# Revit family: URA SPOT Autotest - Permanent_Non Permanent
name_source: partatom
category: Luminaires
units: mm (PartAtom-declared; Revit-internal decimal feet)

## family parameters
Cote de connecteur circulaire = Utiliser le diamètre
Couper avec des vides une fois chargée = Non
Hôte = Face
Partagée = Non
Repere pour localisation dans la piece = Non
Source d'éclairage = Non
Type d'élément = Normal

## types (5) — shared parameters
Alimentation de secours = Autonome (batterie individuelle)
Classe de protection = II
Conditions Générale d'Utilisation = https://export.legrand.com
Consommation en veille = 0.0 mA
Couleur = Blanc
Diamètre = 125 mm
Elévation par défaut = 2300 mm
Fabricant = LEGRAND
Fonction = Éclairage d'évacuation et d'ambiance
Fréquence = 50-60
Hauteur = 45 mm
Hauteur encastrement = 42 mm
IK = 07
IP = 42
Matière = Plastique
Mode de pose = Encastré
Objet Connecté = Non
Puissance du système = 2 W
Temperature d'utilisation MIN-MAX = -5-35
Tension = 230 AC/DC
Type de connexion = Raccordement à vis
Type de pictogramme = autre
URL = https://www.legrand.com
capacité des bornes = 1,5-2,5
source lumineuse = LED non interchangeable
état des accus = NiMh

## per-type parameters (varying)
| type | Autonomie | Batterie de rechange | Désignation produit | Flux lumineux utile | Référence / Modèle | Système de contrôle | Type de commutation |
| 100LM-1H | 1H | 660182 | BAES U22ROND ENCASTRE PERMANENT - NON PERMANENT 100 LUMENS 1H AUTOTEST | 100 lm | LG-660142 | Auto-test automatique | Permanent |
| 200LM-1H | 1H | 660182 | BAES U22ROND ENCASTRE PERMANENT - NON PERMANENT 200 LUMENS 1H AUTOTEST | 200 lm | LG-660144 | Auto-test automatique | Permanent |
| 350LM-1H | 1H | 660184 | BAES U22ROND ENCASTRE PERMANENT - NON PERMANENT 350 LUMENS 1H AUTOTEST | 350 lm | LG-660145 | Auto-test automatique | Permanent |
| 100LM-3H | 3H | 660182 | BAES U22ROND  PERMANENT NON PERMANENT 100 LUMENS 3 H AUTOTEST | 100 lm | LG-660146 | sans | Non permanent |
| 200LM-2H | 2H | 660184 | BAES U22ROND ENCASTRE PERMANENT - NON PERMANENT 200 LUMENS 2H AUTOTEST | 200 lm | LG-660147 | Auto-test automatique | Permanent |
